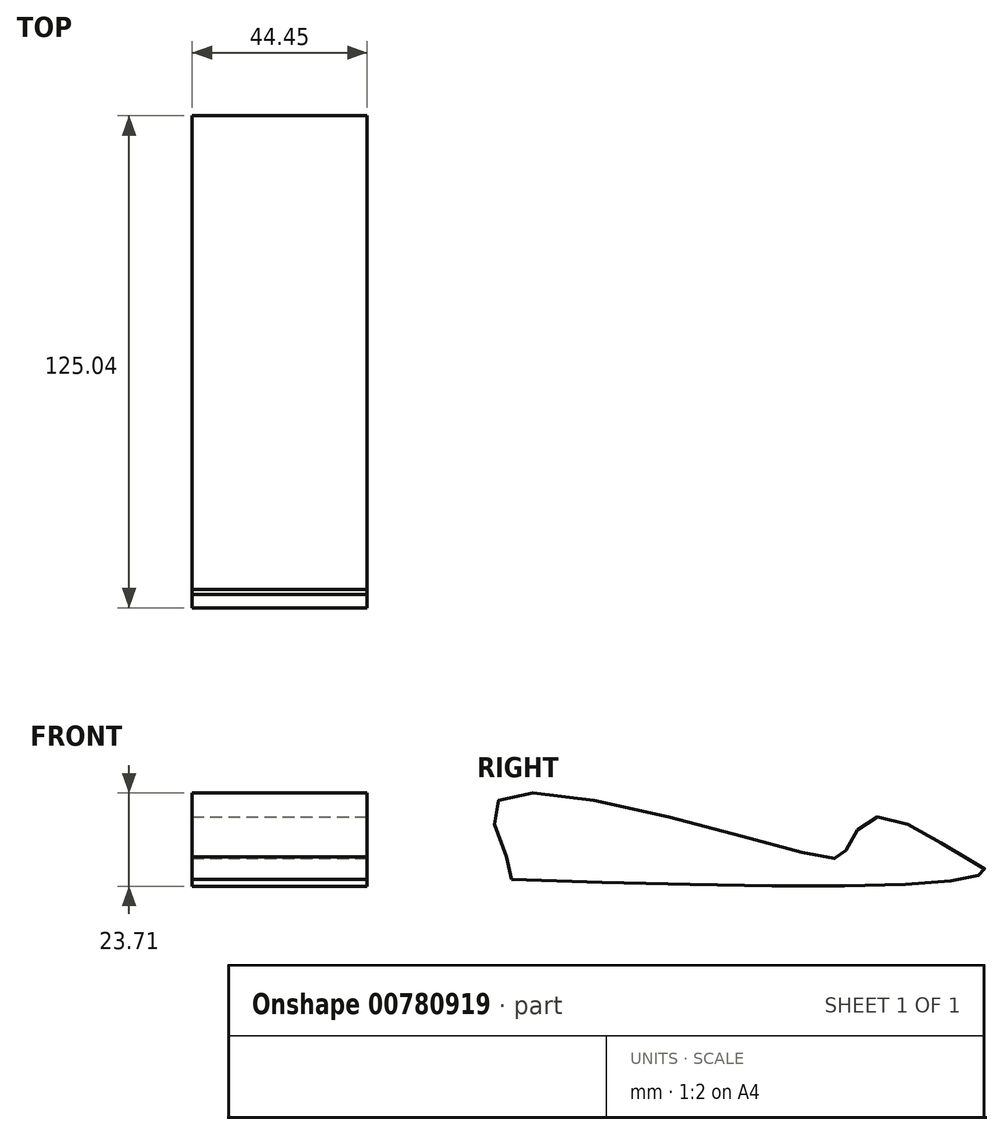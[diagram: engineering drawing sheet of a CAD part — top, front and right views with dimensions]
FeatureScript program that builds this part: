
annotation { "Feature Type Name" : "Feature", "Feature Type Description" : "" }
export const myFeature = defineFeature(function(context is Context, id is Id, definition is map)
    precondition{}
    {
        {
            var Q0;
            Q0=qCreatedBy(makeId("Right.planeOp"),FACE);
            var sketch = newSketch(context, id + "F0", { "sketchPlane" : qUnion([Q0])});
            skFitSpline(sketch, "E0", {"points": [v(-54.1, -12.9) * mm, v(-54.69, 2.46) * mm, v(26.3, -12.9) * mm, v(31.83, -11.53) * mm, v(39.32, -2.86) * mm, v(61.78, -12.71) * mm, v(67.5, -16.26) * mm, v(60.2, -18.82) * mm, v(-52.91, -18.62) * mm], "startDerivative": vector(-87.55, 199.42) * mm, "endDerivative": vector(-533.73, 15.86) * mm});
            skLineSegment(sketch, "E1", {"start": v(-54.1, -12.9) * mm, "end": v(-52.91, -18.62) * mm});
            skSolve(sketch);
        }
        {
            var Q0;
            Q0=makeQuery(id+"F0.imprint","IMPRINT",FACE,{"disambiguationData":[TD([[makeQuery(id+"F0.imprint","IMPRINT",EDGE,{"derivedFrom":sQuery(id+"F0.wireOp",EDGE,"E0")}),-1.0]])]});
            extrude(context, id + "F1", {"entities" : qUnion([Q0]), "depth" : 44.45 * mm, "offsetDistance" : 25.4 * mm});
        }
    });
